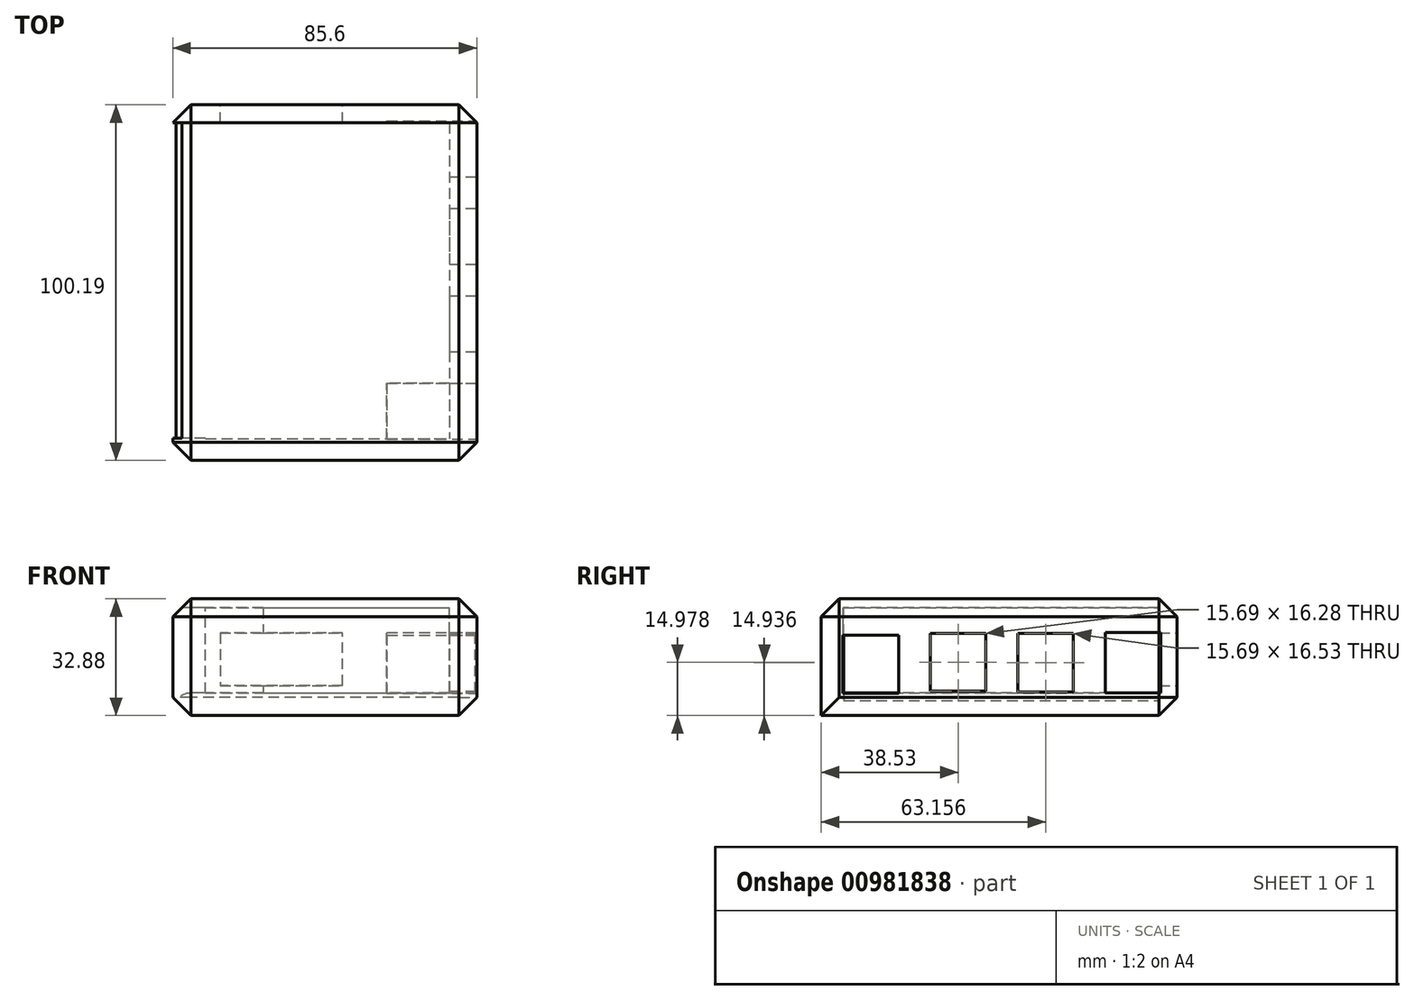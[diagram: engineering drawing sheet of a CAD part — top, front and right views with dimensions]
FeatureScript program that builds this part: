
annotation { "Feature Type Name" : "Feature", "Feature Type Description" : "" }
export const myFeature = defineFeature(function(context is Context, id is Id, definition is map)
    precondition{}
    {
        {
            var Q0;
            Q0=qCreatedBy(makeId("Top.planeOp"),FACE);
            var sketch = newSketch(context, id + "F0", { "sketchPlane" : qUnion([Q0])});
            skLineSegment(sketch, "E0.bottom", {"start": v(-39.22, 75.56) * mm, "end": v(29.53, 75.56) * mm});
            skLineSegment(sketch, "E0.top", {"start": v(-39.22, -13.4) * mm, "end": v(29.53, -13.4) * mm});
            skLineSegment(sketch, "E0.left", {"start": v(-39.22, 75.56) * mm, "end": v(-39.22, -13.4) * mm});
            skLineSegment(sketch, "E0.right", {"start": v(29.53, 75.56) * mm, "end": v(29.53, -13.4) * mm});
            skSolve(sketch);
        }
        {
            var Q0;
            Q0=makeQuery(id+"F0.imprint","IMPRINT",FACE,{"disambiguationData":[TD([[makeQuery(id+"F0.imprint","IMPRINT",EDGE,{"derivedFrom":sQuery(id+"F0.wireOp",EDGE,"E0.bottom")}),-1.0]])]});
            var sketch = newSketch(context, id + "F1", { "sketchPlane" : qUnion([Q0])});
            skLineSegment(sketch, "E1.bottom", {"start": v(-48.37, -19.52) * mm, "end": v(37.23, -19.52) * mm});
            skLineSegment(sketch, "E1.top", {"start": v(-48.37, 80.67) * mm, "end": v(37.23, 80.67) * mm});
            skLineSegment(sketch, "E1.left", {"start": v(-48.37, -19.52) * mm, "end": v(-48.37, 80.67) * mm});
            skLineSegment(sketch, "E1.right", {"start": v(37.23, -19.52) * mm, "end": v(37.23, 80.67) * mm});
            skSolve(sketch);
        }
        {
            var Q0;
            Q0=makeQuery(id+"F1.imprint","IMPRINT",FACE,{"disambiguationData":[TD([[makeQuery(id+"F1.imprint","IMPRINT",EDGE,{"derivedFrom":sQuery(id+"F1.wireOp",EDGE,"E1.bottom")}),1.0]])]});
            extrude(context, id + "F2", {"entities" : qUnion([Q0]), "oppositeDirection" : true, "depth" : 24 * mm, "offsetDistance" : 25.4 * mm});
        }
        {
            var Q0;
            Q0=makeQuery(id+"F2.opExtrude","SWEPT_FACE",FACE,{"disambiguationData":[OSD([sQuery(id+"F1.wireOp",EDGE,"E1.left")])]});
            var sketch = newSketch(context, id + "F3", { "sketchPlane" : qUnion([Q0])});
            skLineSegment(sketch, "E2.bottom", {"start": v(13.23, -24) * mm, "end": v(-75.57, -24) * mm});
            skLineSegment(sketch, "E2.top", {"start": v(13.23, 0) * mm, "end": v(-75.57, 0) * mm});
            skLineSegment(sketch, "E2.left", {"start": v(13.23, -24) * mm, "end": v(13.23, 0) * mm});
            skLineSegment(sketch, "E2.right", {"start": v(-75.57, -24) * mm, "end": v(-75.57, 0) * mm});
            skSolve(sketch);
        }
        {
            var Q0;
            Q0=qSketchRegion(id+"F3",true);
            extrude(context, id + "F4", {"entities" : qUnion([Q0]), "operationType" : NewBodyOperationType.REMOVE, "oppositeDirection" : true, "depth" : 25.4 * mm, "offsetDistance" : 25.4 * mm});
        }
        {
            var Q0;
            Q0=makeQuery(id+"F2.opExtrude","CAP_FACE",FACE,{"disambiguationData":[OSD([sQuery(id+"F0.wireOp",EDGE,"E0.bottom"),sQuery(id+"F0.wireOp",EDGE,"E0.top"),sQuery(id+"F0.wireOp",EDGE,"E0.left"),sQuery(id+"F0.wireOp",EDGE,"E0.right"),sQuery(id+"F1.wireOp",EDGE,"E1.bottom"),sQuery(id+"F1.wireOp",EDGE,"E1.top"),sQuery(id+"F1.wireOp",EDGE,"E1.left"),sQuery(id+"F1.wireOp",EDGE,"E1.right")])],"isStart":false});
            var sketch = newSketch(context, id + "F5", { "sketchPlane" : qUnion([Q0])});
            skLineSegment(sketch, "E3.bottom", {"start": v(37.23, 19.52) * mm, "end": v(-48.37, 19.52) * mm});
            skLineSegment(sketch, "E3.top", {"start": v(37.23, -80.67) * mm, "end": v(-48.37, -80.67) * mm});
            skLineSegment(sketch, "E3.left", {"start": v(37.23, 19.52) * mm, "end": v(37.23, -80.67) * mm});
            skLineSegment(sketch, "E3.right", {"start": v(-48.37, 19.52) * mm, "end": v(-48.37, -80.67) * mm});
            skSolve(sketch);
        }
        {
            var Q0;
            Q0=qSketchRegion(id+"F5",true);
            extrude(context, id + "F6", {"entities" : qUnion([Q0]), "operationType" : NewBodyOperationType.ADD, "depth" : 6.35 * mm, "offsetDistance" : 25.4 * mm});
        }
        {
            var Q0;
            Q0=makeQuery(id+"F2.opExtrude","CAP_FACE",FACE,{"disambiguationData":[OSD([sQuery(id+"F0.wireOp",EDGE,"E0.bottom"),sQuery(id+"F0.wireOp",EDGE,"E0.top"),sQuery(id+"F0.wireOp",EDGE,"E0.left"),sQuery(id+"F0.wireOp",EDGE,"E0.right"),sQuery(id+"F1.wireOp",EDGE,"E1.bottom"),sQuery(id+"F1.wireOp",EDGE,"E1.top"),sQuery(id+"F1.wireOp",EDGE,"E1.left"),sQuery(id+"F1.wireOp",EDGE,"E1.right")])],"isStart":true});
            var sketch = newSketch(context, id + "F7", { "sketchPlane" : qUnion([Q0])});
            skLineSegment(sketch, "E4.bottom", {"start": v(37.23, 80.67) * mm, "end": v(-48.37, 80.67) * mm});
            skLineSegment(sketch, "E4.top", {"start": v(37.23, -19.52) * mm, "end": v(-48.37, -19.52) * mm});
            skLineSegment(sketch, "E4.left", {"start": v(37.23, 80.67) * mm, "end": v(37.23, -19.52) * mm});
            skLineSegment(sketch, "E4.right", {"start": v(-48.37, 80.67) * mm, "end": v(-48.37, -19.52) * mm});
            skSolve(sketch);
        }
        {
            var Q0;
            Q0=qSketchRegion(id+"F7",true);
            extrude(context, id + "F8", {"entities" : qUnion([Q0]), "operationType" : NewBodyOperationType.ADD, "depth" : 2.54 * mm, "offsetDistance" : 25.4 * mm});
        }
        {
            var Q0;
            Q0=makeQuery(id+"F8.boolean.opBoolean","MERGE",FACE,{"derivedFrom":[makeQuery(id+"F6.boolean.opBoolean","MERGE",FACE,{"derivedFrom":[makeQuery(id+"F2.opExtrude","SWEPT_FACE",FACE,{"disambiguationData":[OSD([sQuery(id+"F1.wireOp",EDGE,"E1.right")])]}),makeQuery(id+"F6.opExtrude","SWEPT_FACE",FACE,{"disambiguationData":[OSD([sQuery(id+"F5.wireOp",EDGE,"E3.left")])]})]}),makeQuery(id+"F8.opExtrude","SWEPT_FACE",FACE,{"disambiguationData":[OSD([sQuery(id+"F7.wireOp",EDGE,"E4.left")])]})]});
            var sketch = newSketch(context, id + "F9", { "sketchPlane" : qUnion([Q0])});
            skLineSegment(sketch, "E5.bottom", {"start": v(-13.46, -7.65) * mm, "end": v(2.23, -7.65) * mm});
            skLineSegment(sketch, "E5.top", {"start": v(-13.46, -24.09) * mm, "end": v(2.23, -24.09) * mm});
            skLineSegment(sketch, "E5.left", {"start": v(-13.46, -7.65) * mm, "end": v(-13.46, -24.09) * mm});
            skLineSegment(sketch, "E5.right", {"start": v(2.23, -7.65) * mm, "end": v(2.23, -24.09) * mm});
            skLineSegment(sketch, "E6.bottom", {"start": v(11.17, -23.5) * mm, "end": v(26.85, -23.5) * mm});
            skLineSegment(sketch, "E6.top", {"start": v(11.17, -7.22) * mm, "end": v(26.85, -7.22) * mm});
            skLineSegment(sketch, "E6.left", {"start": v(11.17, -23.5) * mm, "end": v(11.17, -7.22) * mm});
            skLineSegment(sketch, "E6.right", {"start": v(26.85, -23.5) * mm, "end": v(26.85, -7.22) * mm});
            skLineSegment(sketch, "E7.bottom", {"start": v(35.8, -7.14) * mm, "end": v(51.48, -7.14) * mm});
            skLineSegment(sketch, "E7.top", {"start": v(35.8, -23.67) * mm, "end": v(51.48, -23.67) * mm});
            skLineSegment(sketch, "E7.left", {"start": v(35.8, -7.14) * mm, "end": v(35.8, -23.67) * mm});
            skLineSegment(sketch, "E7.right", {"start": v(51.48, -7.14) * mm, "end": v(51.48, -23.67) * mm});
            skLineSegment(sketch, "E8.bottom", {"start": v(60.42, -23.92) * mm, "end": v(76.1, -23.92) * mm});
            skLineSegment(sketch, "E8.top", {"start": v(60.42, -6.97) * mm, "end": v(76.1, -6.97) * mm});
            skLineSegment(sketch, "E8.left", {"start": v(60.42, -23.92) * mm, "end": v(60.42, -6.97) * mm});
            skLineSegment(sketch, "E8.right", {"start": v(76.1, -23.92) * mm, "end": v(76.1, -6.97) * mm});
            skSolve(sketch);
        }
        {
            var Q0;
            Q0=makeQuery(id+"F8.boolean.opBoolean","MERGE",FACE,{"derivedFrom":[makeQuery(id+"F6.boolean.opBoolean","MERGE",FACE,{"derivedFrom":[makeQuery(id+"F2.opExtrude","SWEPT_FACE",FACE,{"disambiguationData":[OSD([sQuery(id+"F1.wireOp",EDGE,"E1.top")])]}),makeQuery(id+"F6.opExtrude","SWEPT_FACE",FACE,{"disambiguationData":[OSD([sQuery(id+"F5.wireOp",EDGE,"E3.top")])]})]}),makeQuery(id+"F8.opExtrude","SWEPT_FACE",FACE,{"disambiguationData":[OSD([sQuery(id+"F7.wireOp",EDGE,"E4.bottom")])]})]});
            var sketch = newSketch(context, id + "F10", { "sketchPlane" : qUnion([Q0])});
            skLineSegment(sketch, "E9.bottom", {"start": v(0.54, -7.07) * mm, "end": v(35.08, -7.07) * mm});
            skLineSegment(sketch, "E9.top", {"start": v(0.54, -21.88) * mm, "end": v(35.08, -21.88) * mm});
            skLineSegment(sketch, "E9.left", {"start": v(0.54, -7.07) * mm, "end": v(0.54, -21.88) * mm});
            skLineSegment(sketch, "E9.right", {"start": v(35.08, -7.07) * mm, "end": v(35.08, -21.88) * mm});
            skSolve(sketch);
        }
        {
            var Q0;
            Q0=qSketchRegion(id+"F10",true);
            var Q1;
            Q1=makeQuery(id+"F10.imprint","IMPRINT",FACE,{"disambiguationData":[TD([[makeQuery(id+"F10.imprint","IMPRINT",EDGE,{"derivedFrom":sQuery(id+"F10.wireOp",EDGE,"E9.bottom")}),-1.0]])]});
            extrude(context, id + "F11", {"entities" : qUnion([Q0, Q1]), "operationType" : NewBodyOperationType.REMOVE, "oppositeDirection" : true, "depth" : 25.4 * mm, "offsetDistance" : 25.4 * mm});
        }
        {
            var Q0;
            Q0=makeQuery(id+"F9.imprint","IMPRINT",FACE,{"disambiguationData":[TD([[makeQuery(id+"F9.imprint","IMPRINT",EDGE,{"derivedFrom":sQuery(id+"F9.wireOp",EDGE,"E8.bottom")}),1.0]])]});
            var Q1;
            Q1=makeQuery(id+"F9.imprint","IMPRINT",FACE,{"disambiguationData":[TD([[makeQuery(id+"F9.imprint","IMPRINT",EDGE,{"derivedFrom":sQuery(id+"F9.wireOp",EDGE,"E7.bottom")}),-1.0]])]});
            var Q2;
            Q2=makeQuery(id+"F9.imprint","IMPRINT",FACE,{"disambiguationData":[TD([[makeQuery(id+"F9.imprint","IMPRINT",EDGE,{"derivedFrom":sQuery(id+"F9.wireOp",EDGE,"E6.bottom")}),1.0]])]});
            var Q3;
            Q3=makeQuery(id+"F9.imprint","IMPRINT",FACE,{"disambiguationData":[TD([[makeQuery(id+"F9.imprint","IMPRINT",EDGE,{"derivedFrom":sQuery(id+"F9.wireOp",EDGE,"E5.bottom")}),-1.0]])]});
            extrude(context, id + "F12", {"entities" : qUnion([Q0, Q1, Q2, Q3]), "operationType" : NewBodyOperationType.REMOVE, "oppositeDirection" : true, "depth" : 25.4 * mm, "offsetDistance" : 25.4 * mm});
        }
        {
            var Q0;
            Q0=makeQuery(id+"F8.opExtrude","CAP_EDGE",EDGE,{"disambiguationData":[OSD([sQuery(id+"F7.wireOp",EDGE,"E4.bottom")])],"isStart":false});
            var Q1;
            Q1=makeQuery(id+"F8.opExtrude","CAP_EDGE",EDGE,{"disambiguationData":[OSD([sQuery(id+"F7.wireOp",EDGE,"E4.left")])],"isStart":false});
            var Q2;
            Q2=makeQuery(id+"F8.opExtrude","CAP_EDGE",EDGE,{"disambiguationData":[OSD([sQuery(id+"F7.wireOp",EDGE,"E4.right")])],"isStart":false});
            var Q3;
            Q3=makeQuery(id+"F8.opExtrude","CAP_EDGE",EDGE,{"disambiguationData":[OSD([sQuery(id+"F7.wireOp",EDGE,"E4.top")])],"isStart":false});
            var Q4;
            Q4=makeQuery(id+"F8.boolean.opBoolean","MERGE",EDGE,{"derivedFrom":[makeQuery(id+"F6.boolean.opBoolean","MERGE",EDGE,{"derivedFrom":[makeQuery(id+"F2.opExtrude","SWEPT_EDGE",EDGE,{"disambiguationData":[OSD([sQuery(id+"F1.wireOp",EDGE,"E1.bottom"),sQuery(id+"F1.wireOp",EDGE,"E1.left")])]}),makeQuery(id+"F6.opExtrude","SWEPT_EDGE",EDGE,{"disambiguationData":[OSD([sQuery(id+"F5.wireOp",EDGE,"E3.bottom"),sQuery(id+"F5.wireOp",EDGE,"E3.right")])]})]}),makeQuery(id+"F8.opExtrude","SWEPT_EDGE",EDGE,{"disambiguationData":[OSD([sQuery(id+"F7.wireOp",EDGE,"E4.top"),sQuery(id+"F7.wireOp",EDGE,"E4.right")])]})]});
            var Q5;
            Q5=makeQuery(id+"F6.opExtrude","CAP_EDGE",EDGE,{"disambiguationData":[OSD([sQuery(id+"F5.wireOp",EDGE,"E3.right")])],"isStart":false});
            var Q6;
            Q6=makeQuery(id+"F8.boolean.opBoolean","MERGE",EDGE,{"derivedFrom":[makeQuery(id+"F6.boolean.opBoolean","MERGE",EDGE,{"derivedFrom":[makeQuery(id+"F2.opExtrude","SWEPT_EDGE",EDGE,{"disambiguationData":[OSD([sQuery(id+"F1.wireOp",EDGE,"E1.top"),sQuery(id+"F1.wireOp",EDGE,"E1.left")])]}),makeQuery(id+"F6.opExtrude","SWEPT_EDGE",EDGE,{"disambiguationData":[OSD([sQuery(id+"F5.wireOp",EDGE,"E3.top"),sQuery(id+"F5.wireOp",EDGE,"E3.right")])]})]}),makeQuery(id+"F8.opExtrude","SWEPT_EDGE",EDGE,{"disambiguationData":[OSD([sQuery(id+"F7.wireOp",EDGE,"E4.bottom"),sQuery(id+"F7.wireOp",EDGE,"E4.right")])]})]});
            var Q7;
            Q7=makeQuery(id+"F8.boolean.opBoolean","MERGE",EDGE,{"derivedFrom":[makeQuery(id+"F6.boolean.opBoolean","MERGE",EDGE,{"derivedFrom":[makeQuery(id+"F2.opExtrude","SWEPT_EDGE",EDGE,{"disambiguationData":[OSD([sQuery(id+"F1.wireOp",EDGE,"E1.top"),sQuery(id+"F1.wireOp",EDGE,"E1.right")])]}),makeQuery(id+"F6.opExtrude","SWEPT_EDGE",EDGE,{"disambiguationData":[OSD([sQuery(id+"F5.wireOp",EDGE,"E3.top"),sQuery(id+"F5.wireOp",EDGE,"E3.left")])]})]}),makeQuery(id+"F8.opExtrude","SWEPT_EDGE",EDGE,{"disambiguationData":[OSD([sQuery(id+"F7.wireOp",EDGE,"E4.bottom"),sQuery(id+"F7.wireOp",EDGE,"E4.left")])]})]});
            var Q8;
            Q8=makeQuery(id+"F6.opExtrude","CAP_EDGE",EDGE,{"disambiguationData":[OSD([sQuery(id+"F5.wireOp",EDGE,"E3.top")])],"isStart":false});
            var Q9;
            Q9=makeQuery(id+"F6.opExtrude","CAP_EDGE",EDGE,{"disambiguationData":[OSD([sQuery(id+"F5.wireOp",EDGE,"E3.left")])],"isStart":false});
            var Q10;
            Q10=makeQuery(id+"F8.boolean.opBoolean","MERGE",EDGE,{"derivedFrom":[makeQuery(id+"F6.boolean.opBoolean","MERGE",EDGE,{"derivedFrom":[makeQuery(id+"F2.opExtrude","SWEPT_EDGE",EDGE,{"disambiguationData":[OSD([sQuery(id+"F1.wireOp",EDGE,"E1.bottom"),sQuery(id+"F1.wireOp",EDGE,"E1.right")])]}),makeQuery(id+"F6.opExtrude","SWEPT_EDGE",EDGE,{"disambiguationData":[OSD([sQuery(id+"F5.wireOp",EDGE,"E3.bottom"),sQuery(id+"F5.wireOp",EDGE,"E3.left")])]})]}),makeQuery(id+"F8.opExtrude","SWEPT_EDGE",EDGE,{"disambiguationData":[OSD([sQuery(id+"F7.wireOp",EDGE,"E4.top"),sQuery(id+"F7.wireOp",EDGE,"E4.left")])]})]});
            chamfer(context, id + "F13", {"entities" : qUnion([Q0, Q1, Q2, Q3, Q4, Q5, Q6, Q7, Q8, Q9, Q10]), "width" : 5.08 * mm, "tangentPropagation" : true});
        }
        {
            var Q0;
            Q0=makeQuery(id+"F11.boolean.opBoolean","COPY",EDGE,{"derivedFrom":makeQuery(id+"F11.opExtrude","CAP_EDGE",EDGE,{"disambiguationData":[OSD([sQuery(id+"F10.wireOp",EDGE,"E9.top")])],"isStart":true})});
            var Q1;
            Q1=makeQuery(id+"F12.boolean.opBoolean","COPY",EDGE,{"derivedFrom":makeQuery(id+"F12.opExtrude","CAP_EDGE",EDGE,{"disambiguationData":[OSD([sQuery(id+"F9.wireOp",EDGE,"E8.bottom")])],"isStart":true})});
            var Q2;
            Q2=makeQuery(id+"F12.boolean.opBoolean","COPY",EDGE,{"derivedFrom":makeQuery(id+"F12.opExtrude","CAP_EDGE",EDGE,{"disambiguationData":[OSD([sQuery(id+"F9.wireOp",EDGE,"E7.top")])],"isStart":true})});
            var Q3;
            Q3=makeQuery(id+"F12.boolean.opBoolean","COPY",EDGE,{"derivedFrom":makeQuery(id+"F12.opExtrude","CAP_EDGE",EDGE,{"disambiguationData":[OSD([sQuery(id+"F9.wireOp",EDGE,"E6.bottom")])],"isStart":true})});
            var Q4;
            Q4=makeQuery(id+"F12.boolean.opBoolean","COPY",EDGE,{"derivedFrom":makeQuery(id+"F12.opExtrude","CAP_EDGE",EDGE,{"disambiguationData":[OSD([sQuery(id+"F9.wireOp",EDGE,"E5.top")])],"isStart":true})});
            var Q5;
            Q5=makeQuery(id+"F6.opExtrude","CAP_EDGE",EDGE,{"disambiguationData":[OSD([sQuery(id+"F5.wireOp",EDGE,"E3.right")])],"isStart":true});
            fillet(context, id + "F14", {"entities" : qUnion([Q0, Q1, Q2, Q3, Q4, Q5]), "radius" : 5.08 * mm, "tangentPropagation" : true, "allowEdgeOverflow" : false});
        }
    });
